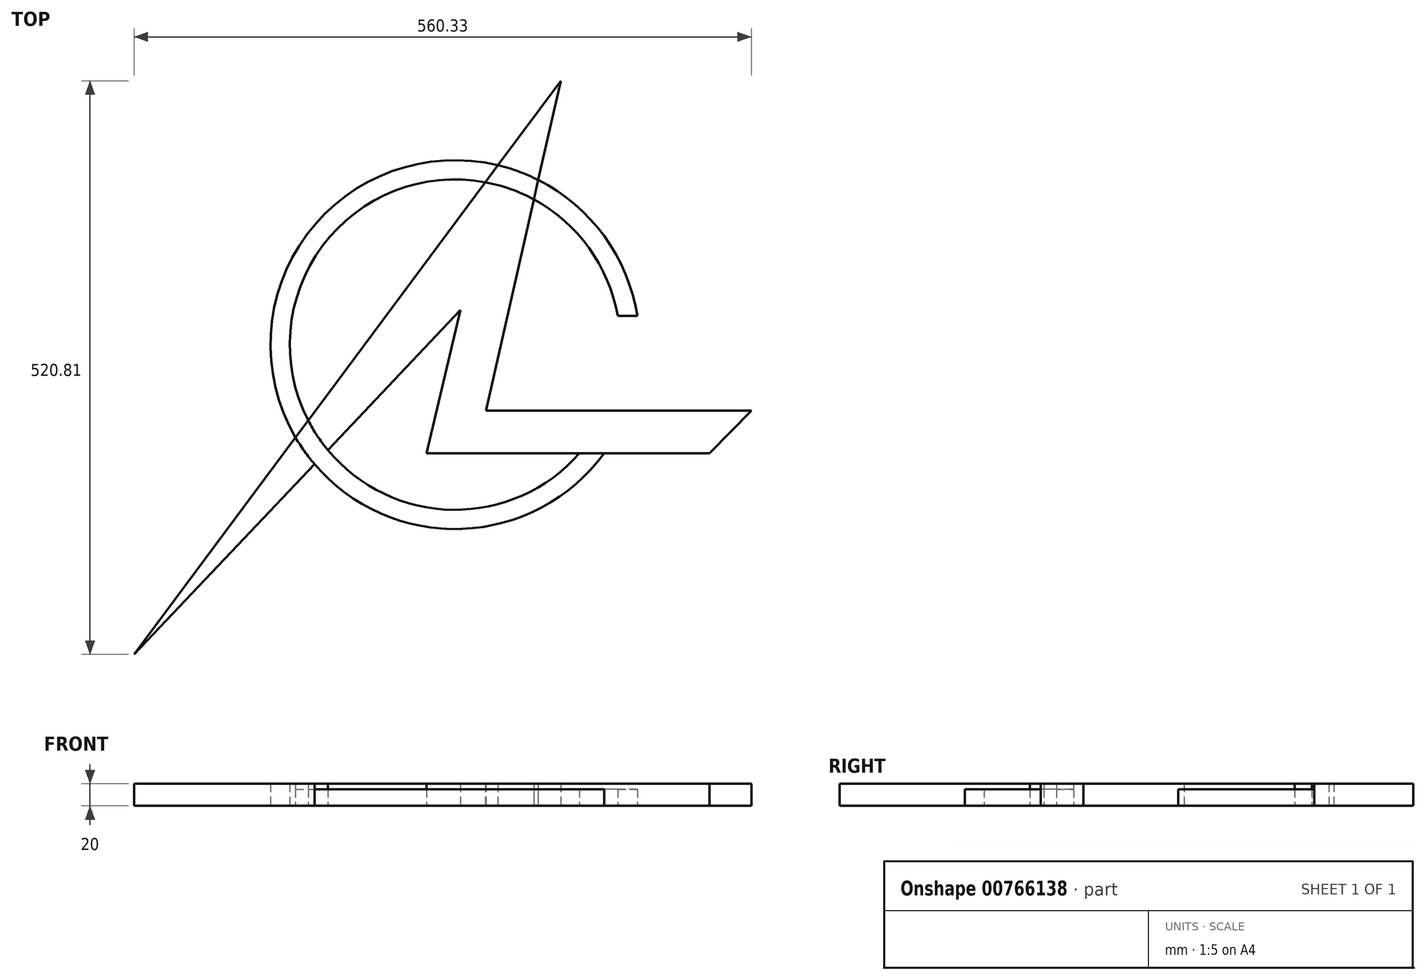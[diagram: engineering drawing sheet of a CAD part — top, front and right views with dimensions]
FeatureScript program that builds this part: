
annotation { "Feature Type Name" : "Feature", "Feature Type Description" : "" }
export const myFeature = defineFeature(function(context is Context, id is Id, definition is map)
    precondition{}
    {
        {
            var Q0;
            Q0=qCreatedBy(makeId("Top.planeOp"),FACE);
            var sketch = newSketch(context, id + "F0", { "sketchPlane" : qUnion([Q0])});
            skCircle(sketch, "E0", {"center": v(0, 0) * mm, "radius": 150 * mm});
            skCircle(sketch, "E1", {"center": v(0, 0) * mm, "radius": 167.5 * mm});
            skLineSegment(sketch, "E2", {"start": v(28, -59.92) * mm, "end": v(269, -59.92) * mm});
            skLineSegment(sketch, "E3", {"start": v(269, -59.92) * mm, "end": v(231.03, -98.76) * mm});
            skLineSegment(sketch, "E4", {"start": v(231.03, -98.76) * mm, "end": v(-24.5, -98.76) * mm});
            skLineSegment(sketch, "E5", {"start": v(-24.5, -98.76) * mm, "end": v(-25.97, -98.76) * mm});
            skLineSegment(sketch, "E6", {"start": v(-25.97, -98.76) * mm, "end": v(5.04, 31.6) * mm});
            skLineSegment(sketch, "E7", {"start": v(5.04, 31.6) * mm, "end": v(-291.33, -281.33) * mm});
            skLineSegment(sketch, "E8", {"start": v(-291.33, -281.33) * mm, "end": v(95.92, 239.48) * mm});
            skLineSegment(sketch, "E9", {"start": v(95.92, 239.48) * mm, "end": v(28, -59.92) * mm});
            skLineSegment(sketch, "E10", {"start": v(49.43, -46.41) * mm, "end": v(65.44, 25.88) * mm});
            skLineSegment(sketch, "E11", {"start": v(65.44, 25.88) * mm, "end": v(84.44, 25.88) * mm});
            skLineSegment(sketch, "E12", {"start": v(84.44, 25.88) * mm, "end": v(70.86, -32.87) * mm});
            skLineSegment(sketch, "E13", {"start": v(70.86, -32.87) * mm, "end": v(106.77, -32.87) * mm});
            skLineSegment(sketch, "E14", {"start": v(106.77, -32.87) * mm, "end": v(101.6, -46.41) * mm});
            skLineSegment(sketch, "E15", {"start": v(101.6, -46.41) * mm, "end": v(49.43, -46.41) * mm});
            skLineSegment(sketch, "E16", {"start": v(122.27, 26.2) * mm, "end": v(140.97, 26.2) * mm});
            skLineSegment(sketch, "E17", {"start": v(140.97, 26.2) * mm, "end": v(168.2, 26.2) * mm});
            skLineSegment(sketch, "E18", {"start": v(168.2, 26.2) * mm, "end": v(186.04, 26.2) * mm});
            skLineSegment(sketch, "E19", {"start": v(186.04, 26.2) * mm, "end": v(174.24, -28.08) * mm});
            skLineSegment(sketch, "E20", {"start": v(168.2, 26.2) * mm, "end": v(157.73, -22.5) * mm});
            skSolve(sketch);
        }
        {
            var Q0;
            {var subQ13=sQuery(id+"F0.wireOp",EDGE,"E5");Q0=makeQuery(id+"F0.imprint","IMPRINT",FACE,{"disambiguationData":[TD([[makeQuery(id+"F0.imprint","IMPRINT",EDGE,{"derivedFrom":subQ13}),-1.0]])]});}
            var Q1;
            {var subQ0=sQuery(id+"F0.wireOp",EDGE,"E8");var subQ1=sQuery(id+"F0.wireOp",EDGE,"E0");var subQ2=makeQuery(id+"F0.imprint","INTERSECT",VERTEX,{"disambiguationData":[OD(0.0)],"derivedFrom":[subQ1,subQ0]});Q1=makeQuery(id+"F0.imprint","IMPRINT",FACE,{"disambiguationData":[TD([[makeQuery(id+"F0.imprint","IMPRINT",EDGE,{"disambiguationData":[TD([[subQ2,1.0]])],"derivedFrom":subQ1}),-1.0]])]});}
            var Q2;
            {var subQ0=sQuery(id+"F0.wireOp",EDGE,"E8");var subQ1=sQuery(id+"F0.wireOp",EDGE,"E1");var subQ2=makeQuery(id+"F0.imprint","INTERSECT",VERTEX,{"disambiguationData":[OD(0.0)],"derivedFrom":[subQ1,subQ0]});Q2=makeQuery(id+"F0.imprint","IMPRINT",FACE,{"disambiguationData":[TD([[makeQuery(id+"F0.imprint","IMPRINT",EDGE,{"disambiguationData":[TD([[subQ2,1.0]])],"derivedFrom":subQ1}),-1.0]])]});}
            var Q3;
            {var subQ5=sQuery(id+"F0.wireOp",EDGE,"E3");Q3=makeQuery(id+"F0.imprint","IMPRINT",FACE,{"disambiguationData":[TD([[makeQuery(id+"F0.imprint","IMPRINT",EDGE,{"derivedFrom":subQ5}),-1.0]])]});}
            var Q4;
            {var subQ0=sQuery(id+"F0.wireOp",EDGE,"E4");var subQ1=sQuery(id+"F0.wireOp",EDGE,"E0");var subQ2=makeQuery(id+"F0.imprint","INTERSECT",VERTEX,{"derivedFrom":[subQ1,subQ0]});Q4=makeQuery(id+"F0.imprint","IMPRINT",FACE,{"disambiguationData":[TD([[makeQuery(id+"F0.imprint","IMPRINT",EDGE,{"disambiguationData":[TD([[subQ2,-1.0]])],"derivedFrom":subQ1}),-1.0]])]});}
            var Q5;
            {var subQ0=sQuery(id+"F0.wireOp",EDGE,"E8");var subQ1=sQuery(id+"F0.wireOp",EDGE,"E1");var subQ2=makeQuery(id+"F0.imprint","INTERSECT",VERTEX,{"disambiguationData":[OD(1.0)],"derivedFrom":[subQ1,subQ0]});Q5=makeQuery(id+"F0.imprint","IMPRINT",FACE,{"disambiguationData":[TD([[makeQuery(id+"F0.imprint","IMPRINT",EDGE,{"disambiguationData":[TD([[subQ2,-1.0]])],"derivedFrom":subQ1}),-1.0]])]});}
            var Q6;
            {var subQ0=sQuery(id+"F0.wireOp",EDGE,"E8");var subQ1=sQuery(id+"F0.wireOp",EDGE,"E0");var subQ2=makeQuery(id+"F0.imprint","INTERSECT",VERTEX,{"disambiguationData":[OD(1.0)],"derivedFrom":[subQ1,subQ0]});Q6=makeQuery(id+"F0.imprint","IMPRINT",FACE,{"disambiguationData":[TD([[makeQuery(id+"F0.imprint","IMPRINT",EDGE,{"disambiguationData":[TD([[subQ2,-1.0]])],"derivedFrom":subQ1}),-1.0]])]});}
            extrude(context, id + "F1", {"entities" : qUnion([Q0, Q1, Q2, Q3, Q4, Q5, Q6]), "depth" : 20 * mm, "offsetDistance" : 25 * mm});
        }
        {
            var Q0;
            {var subQ0=sQuery(id+"F0.wireOp",EDGE,"E8");var subQ1=sQuery(id+"F0.wireOp",EDGE,"E0");var subQ2=makeQuery(id+"F0.imprint","INTERSECT",VERTEX,{"disambiguationData":[OD(0.0)],"derivedFrom":[subQ1,subQ0]});Q0=makeQuery(id+"F0.imprint","IMPRINT",FACE,{"disambiguationData":[TD([[makeQuery(id+"F0.imprint","IMPRINT",EDGE,{"disambiguationData":[TD([[subQ2,-1.0]])],"derivedFrom":subQ1}),-1.0]])]});}
            var Q1;
            {var subQ0=sQuery(id+"F0.wireOp",EDGE,"E9");var subQ1=sQuery(id+"F0.wireOp",EDGE,"E0");var subQ2=makeQuery(id+"F0.imprint","INTERSECT",VERTEX,{"derivedFrom":[subQ1,subQ0]});Q1=makeQuery(id+"F0.imprint","IMPRINT",FACE,{"disambiguationData":[TD([[makeQuery(id+"F0.imprint","IMPRINT",EDGE,{"disambiguationData":[TD([[subQ2,1.0]])],"derivedFrom":subQ1}),-1.0]])]});}
            var Q2;
            {var subQ0=sQuery(id+"F0.wireOp",EDGE,"E7");var subQ1=sQuery(id+"F0.wireOp",EDGE,"E0");var subQ2=makeQuery(id+"F0.imprint","INTERSECT",VERTEX,{"derivedFrom":[subQ1,subQ0]});Q2=makeQuery(id+"F0.imprint","IMPRINT",FACE,{"disambiguationData":[TD([[makeQuery(id+"F0.imprint","IMPRINT",EDGE,{"disambiguationData":[TD([[subQ2,-1.0]])],"derivedFrom":subQ1}),-1.0]])]});}
            extrude(context, id + "F2", {"entities" : qUnion([Q0, Q1, Q2]), "operationType" : NewBodyOperationType.ADD, "depth" : 15 * mm, "offsetDistance" : 25 * mm});
        }
    });
